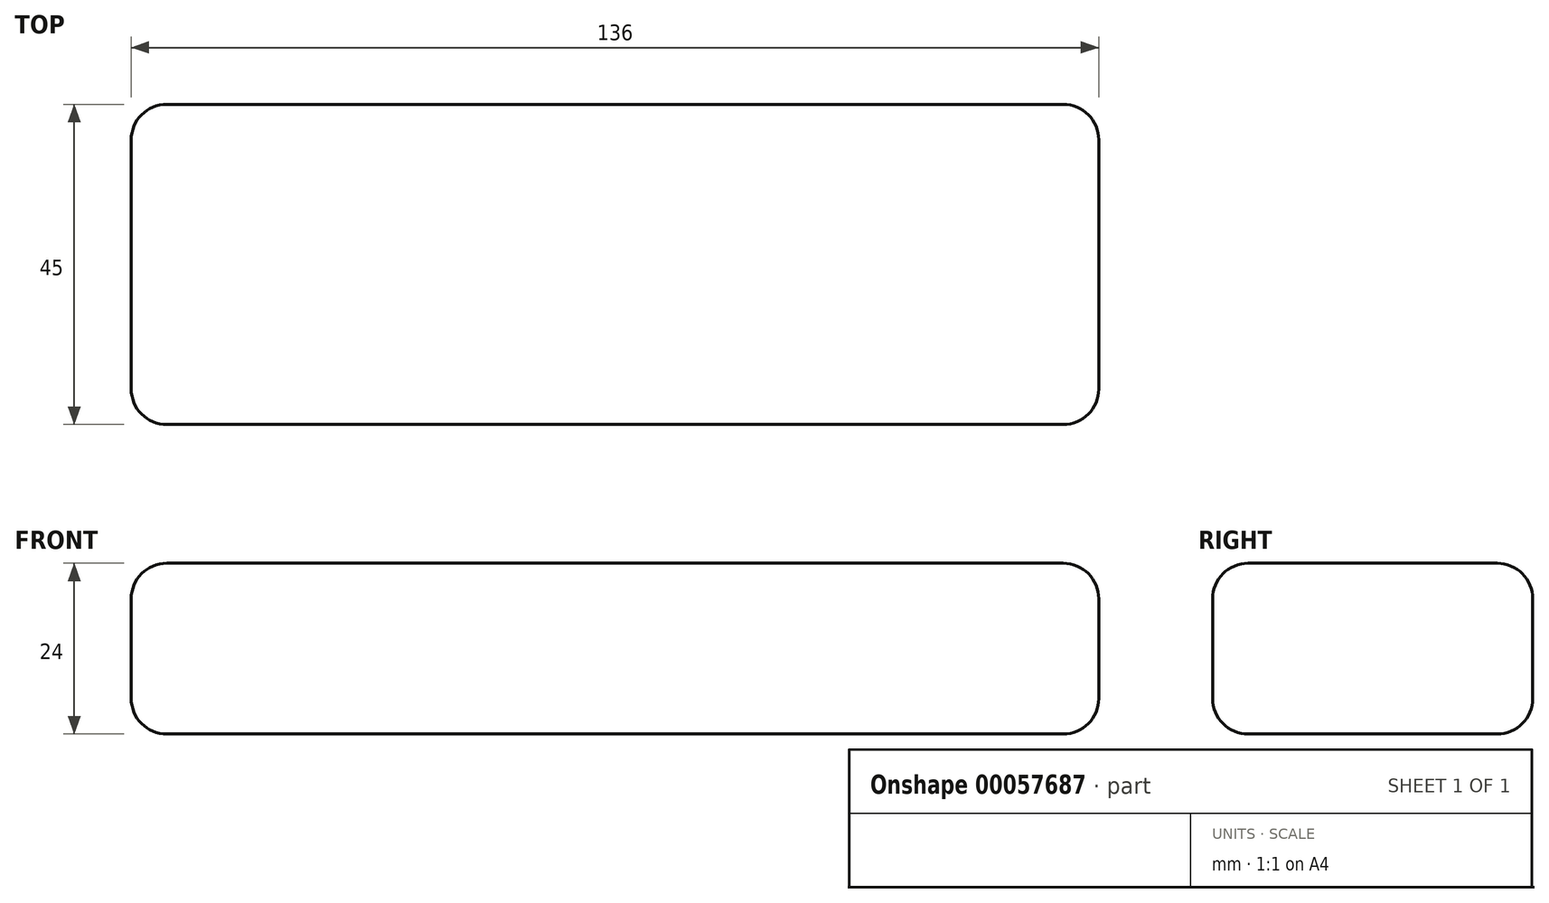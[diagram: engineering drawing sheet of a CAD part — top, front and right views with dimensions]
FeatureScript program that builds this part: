
annotation { "Feature Type Name" : "Feature", "Feature Type Description" : "" }
export const myFeature = defineFeature(function(context is Context, id is Id, definition is map)
    precondition{}
    {
        {
            var Q0;
            Q0=qCreatedBy(makeId("Top.planeOp"),FACE);
            var sketch = newSketch(context, id + "F0", { "sketchPlane" : qUnion([Q0])});
            skLineSegment(sketch, "E0.rect.bottom", {"start": v(68, -22.5) * mm, "end": v(-68, -22.5) * mm});
            skLineSegment(sketch, "E0.rect.top", {"start": v(68, 22.5) * mm, "end": v(-68, 22.5) * mm});
            skLineSegment(sketch, "E0.rect.left", {"start": v(68, -22.5) * mm, "end": v(68, 22.5) * mm});
            skLineSegment(sketch, "E0.rect.right", {"start": v(-68, -22.5) * mm, "end": v(-68, 22.5) * mm});
            skPoint(sketch, "E0.rect.middle", {"position": v(0, 0) * mm});
            skSolve(sketch);
        }
        {
            var Q0;
            Q0=makeQuery(id+"F0.imprint","IMPRINT",FACE,{"disambiguationData":[TD([[makeQuery(id+"F0.imprint","IMPRINT",EDGE,{"derivedFrom":sQuery(id+"F0.wireOp",EDGE,"E0.rect.bottom")}),-1.0]])]});
            extrude(context, id + "F1", {"entities" : qUnion([Q0]), "depth" : 24 * mm});
        }
        {
            var Q0;
            Q0=makeQuery(id+"F1.opExtrude","CAP_EDGE",EDGE,{"disambiguationData":[OSD([sQuery(id+"F0.wireOp",EDGE,"E0.rect.right")])],"isStart":false});
            var Q1;
            Q1=makeQuery(id+"F1.opExtrude","SWEPT_EDGE",EDGE,{"disambiguationData":[OSD([sQuery(id+"F0.wireOp",EDGE,"E0.rect.top"),sQuery(id+"F0.wireOp",EDGE,"E0.rect.right")])]});
            var Q2;
            Q2=makeQuery(id+"F1.opExtrude","SWEPT_EDGE",EDGE,{"disambiguationData":[OSD([sQuery(id+"F0.wireOp",EDGE,"E0.rect.bottom"),sQuery(id+"F0.wireOp",EDGE,"E0.rect.right")])]});
            var Q3;
            Q3=makeQuery(id+"F1.opExtrude","CAP_EDGE",EDGE,{"disambiguationData":[OSD([sQuery(id+"F0.wireOp",EDGE,"E0.rect.right")])],"isStart":true});
            var Q4;
            Q4=makeQuery(id+"F1.opExtrude","CAP_EDGE",EDGE,{"disambiguationData":[OSD([sQuery(id+"F0.wireOp",EDGE,"E0.rect.bottom")])],"isStart":true});
            var Q5;
            Q5=makeQuery(id+"F1.opExtrude","CAP_EDGE",EDGE,{"disambiguationData":[OSD([sQuery(id+"F0.wireOp",EDGE,"E0.rect.bottom")])],"isStart":false});
            var Q6;
            Q6=makeQuery(id+"F1.opExtrude","CAP_EDGE",EDGE,{"disambiguationData":[OSD([sQuery(id+"F0.wireOp",EDGE,"E0.rect.top")])],"isStart":false});
            var Q7;
            Q7=makeQuery(id+"F1.opExtrude","SWEPT_EDGE",EDGE,{"disambiguationData":[OSD([sQuery(id+"F0.wireOp",EDGE,"E0.rect.bottom"),sQuery(id+"F0.wireOp",EDGE,"E0.rect.left")])]});
            var Q8;
            Q8=makeQuery(id+"F1.opExtrude","CAP_EDGE",EDGE,{"disambiguationData":[OSD([sQuery(id+"F0.wireOp",EDGE,"E0.rect.left")])],"isStart":false});
            var Q9;
            Q9=makeQuery(id+"F1.opExtrude","SWEPT_EDGE",EDGE,{"disambiguationData":[OSD([sQuery(id+"F0.wireOp",EDGE,"E0.rect.top"),sQuery(id+"F0.wireOp",EDGE,"E0.rect.left")])]});
            var Q10;
            Q10=makeQuery(id+"F1.opExtrude","CAP_EDGE",EDGE,{"disambiguationData":[OSD([sQuery(id+"F0.wireOp",EDGE,"E0.rect.left")])],"isStart":true});
            var Q11;
            Q11=makeQuery(id+"F1.opExtrude","CAP_EDGE",EDGE,{"disambiguationData":[OSD([sQuery(id+"F0.wireOp",EDGE,"E0.rect.top")])],"isStart":true});
            fillet(context, id + "F2", {"entities" : qUnion([Q0, Q1, Q2, Q3, Q4, Q5, Q6, Q7, Q8, Q9, Q10, Q11]), "radius" : 5 * mm, "tangentPropagation" : true, "allowEdgeOverflow" : false});
        }
    });
